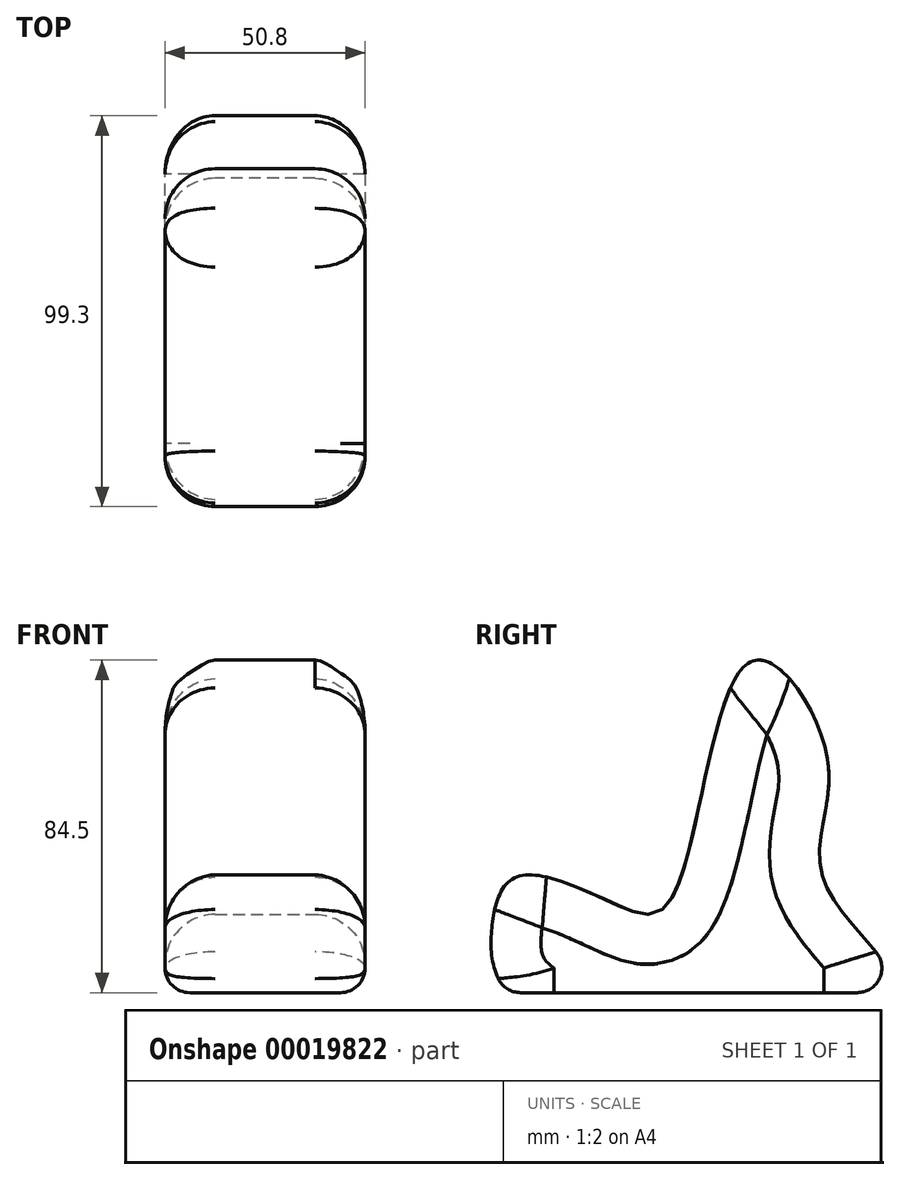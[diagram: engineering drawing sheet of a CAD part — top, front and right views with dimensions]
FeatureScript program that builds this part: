
annotation { "Feature Type Name" : "Feature", "Feature Type Description" : "" }
export const myFeature = defineFeature(function(context is Context, id is Id, definition is map)
    precondition{}
    {
        {
            var Q0;
            Q0=qCreatedBy(makeId("Right.planeOp"),FACE);
            var sketch = newSketch(context, id + "F0", { "sketchPlane" : qUnion([Q0])});
            skFitSpline(sketch, "E0", {"points": [v(-25, 0) * mm, v(-37.38, 22.9) * mm, v(-30.8, 35.88) * mm, v(-6.36, 29) * mm, v(7.85, 29.62) * mm, v(28.28, 90.39) * mm, v(47.93, 65.39) * mm, v(47.43, 33.75) * mm, v(67.88, 0) * mm, v(-25, 0) * mm]});
            skSolve(sketch);
        }
        {
            var Q0;
            Q0=makeQuery(id+"F0.imprint","IMPRINT",FACE,{"disambiguationData":[TD([[makeQuery(id+"F0.imprint","IMPRINT",EDGE,{"derivedFrom":sQuery(id+"F0.wireOp",EDGE,"E0")}),-1.0]])]});
            extrude(context, id + "F1", {"entities" : qUnion([Q0]), "depth" : 25.4 * mm, "hasSecondDirection" : true, "secondDirectionOppositeDirection" : true, "secondDirectionDepth" : 25.4 * mm});
        }
        {
            var Q0;
            Q0=makeQuery(id+"F1.opExtrude","CAP_EDGE",EDGE,{"disambiguationData":[OSD([sQuery(id+"F0.wireOp",EDGE,"E0")])],"isStart":false});
            var Q1;
            Q1=makeQuery(id+"F1.opExtrude","CAP_EDGE",EDGE,{"disambiguationData":[OSD([sQuery(id+"F0.wireOp",EDGE,"E0")])],"isStart":true});
            fillet(context, id + "F2", {"entities" : qUnion([Q0, Q1]), "radius" : 12.7 * mm, "tangentPropagation" : true, "allowEdgeOverflow" : false});
        }
        {
            var Q0;
            Q0=qCreatedBy(makeId("Top.planeOp"),FACE);
            var sketch = newSketch(context, id + "F3", { "sketchPlane" : qUnion([Q0])});
            skLineSegment(sketch, "E1.bottom", {"start": v(-42.51, -50.93) * mm, "end": v(30.7, -50.93) * mm});
            skLineSegment(sketch, "E1.top", {"start": v(-42.51, 86.01) * mm, "end": v(30.7, 86.01) * mm});
            skLineSegment(sketch, "E1.left", {"start": v(-42.51, -50.93) * mm, "end": v(-42.51, 86.01) * mm});
            skLineSegment(sketch, "E1.right", {"start": v(30.7, -50.93) * mm, "end": v(30.7, 86.01) * mm});
            skSolve(sketch);
        }
        {
            var Q0;
            Q0=makeQuery(id+"F3.imprint","IMPRINT",FACE,{"disambiguationData":[TD([[makeQuery(id+"F3.imprint","IMPRINT",EDGE,{"derivedFrom":sQuery(id+"F3.wireOp",EDGE,"E1.bottom")}),1.0]])]});
            extrude(context, id + "F4", {"entities" : qUnion([Q0]), "operationType" : NewBodyOperationType.REMOVE, "depth" : 6.37 * mm, "hasSecondDirection" : true, "secondDirectionOppositeDirection" : true, "secondDirectionDepth" : 25.4 * mm});
        }
        {
            var Q0;
            Q0=makeQuery(id+"F4.boolean.opBoolean","COPY",FACE,{"derivedFrom":makeQuery(id+"F4.opExtrude","CAP_FACE",FACE,{"disambiguationData":[OSD([sQuery(id+"F3.wireOp",EDGE,"E1.bottom"),sQuery(id+"F3.wireOp",EDGE,"E1.top"),sQuery(id+"F3.wireOp",EDGE,"E1.left"),sQuery(id+"F3.wireOp",EDGE,"E1.right")])],"isStart":false})});
            var Q1;
            {var subQ0=sQuery(id+"F0.wireOp",EDGE,"E0");Q1=makeQuery(id+"F4.boolean.opBoolean","INTERSECT",EDGE,{"derivedFrom":[makeQuery(id+"F2.opFillet","BLEND_FACE",FACE,{"disambiguationData":[OSD([subQ0]),TDD([makeQuery(id+"F1.opExtrude","CAP_EDGE",EDGE,{"disambiguationData":[OSD([subQ0])],"isStart":false})]),OD(2.0)]}),makeQuery(id+"F4.opExtrude","CAP_FACE",FACE,{"disambiguationData":[OSD([sQuery(id+"F3.wireOp",EDGE,"E1.bottom"),sQuery(id+"F3.wireOp",EDGE,"E1.top"),sQuery(id+"F3.wireOp",EDGE,"E1.left"),sQuery(id+"F3.wireOp",EDGE,"E1.right")])],"isStart":false})]});}
            fillet(context, id + "F5", {"entities" : qUnion([Q0, Q1]), "radius" : 6.28 * mm, "tangentPropagation" : true, "allowEdgeOverflow" : false});
        }
    });
